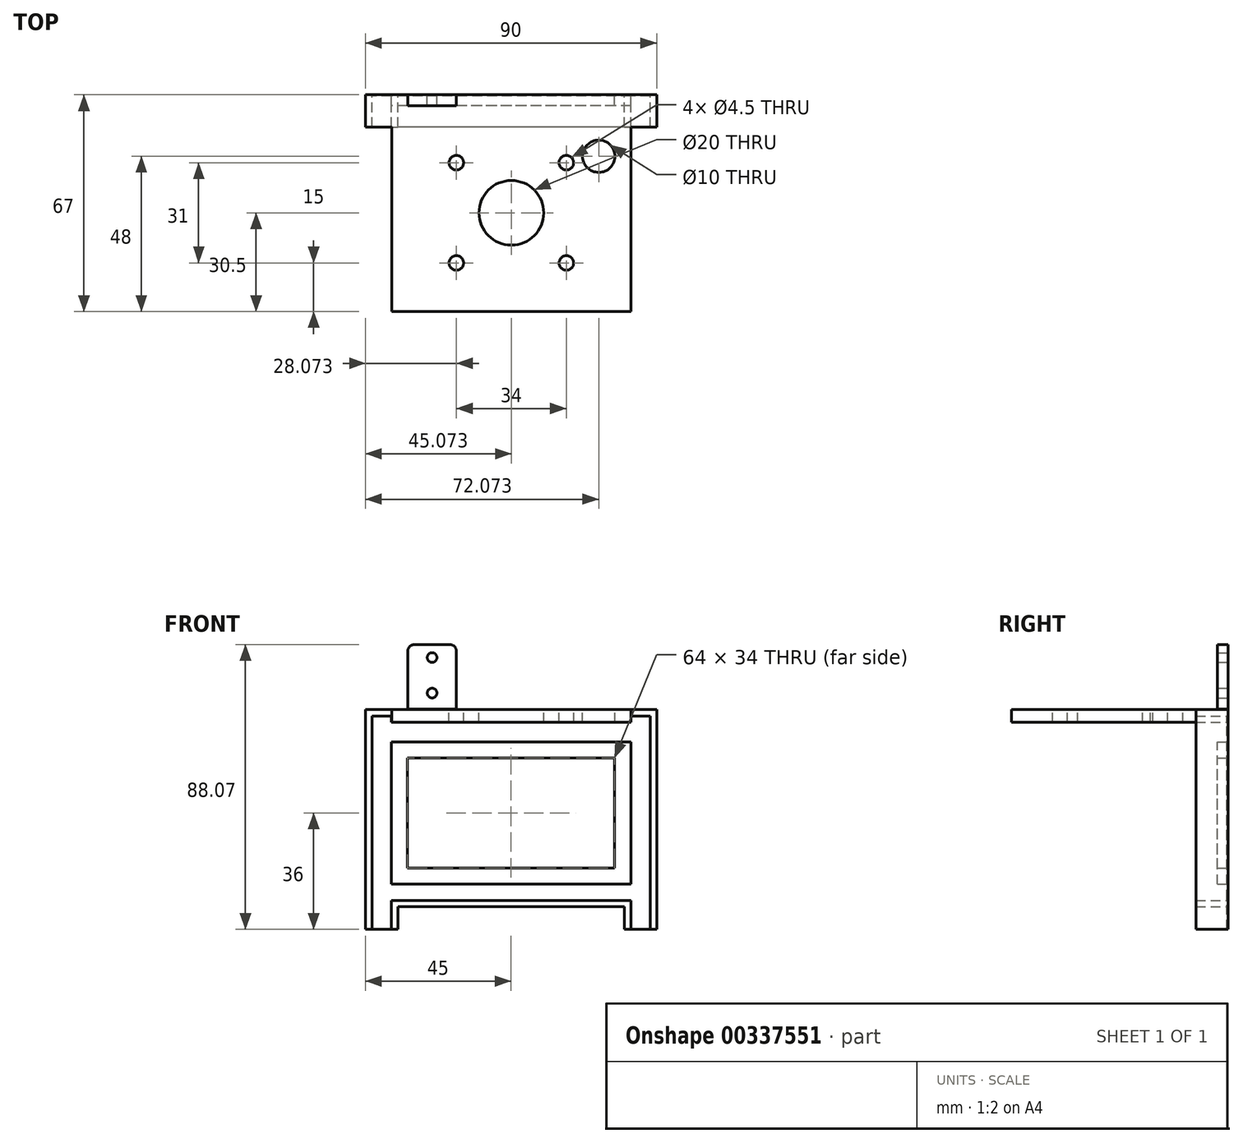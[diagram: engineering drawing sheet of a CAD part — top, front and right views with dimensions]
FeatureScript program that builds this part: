
annotation { "Feature Type Name" : "Feature", "Feature Type Description" : "" }
export const myFeature = defineFeature(function(context is Context, id is Id, definition is map)
    precondition{}
    {
        {
            var Q0;
            Q0=qCreatedBy(makeId("Front.planeOp"),FACE);
            var sketch = newSketch(context, id + "F0", { "sketchPlane" : qUnion([Q0])});
            skLineSegment(sketch, "E0.bottom", {"start": v(-6, -55) * mm, "end": v(-80, -55) * mm});
            skLineSegment(sketch, "E0.top", {"start": v(-6, 0) * mm, "end": v(-80, 0) * mm});
            skLineSegment(sketch, "E0.left", {"start": v(0, -64) * mm, "end": v(0, 2) * mm});
            skLineSegment(sketch, "E0.right", {"start": v(-86, -64) * mm, "end": v(-86, 2) * mm});
            skLineSegment(sketch, "E1.0", {"start": v(0, 2) * mm, "end": v(-6, 2) * mm});
            skLineSegment(sketch, "E2.0", {"start": v(-80, -64) * mm, "end": v(-80, -55) * mm});
            skLineSegment(sketch, "E3.0", {"start": v(-6, -50) * mm, "end": v(-80, -50) * mm});
            skLineSegment(sketch, "E4.0", {"start": v(-6, -64) * mm, "end": v(-6, -55) * mm});
            skLineSegment(sketch, "E5.0", {"start": v(-6, -6) * mm, "end": v(-80, -6) * mm});
            skLineSegment(sketch, "E6.0", {"start": v(0, -64) * mm, "end": v(-6, -64) * mm});
            skPoint(sketch, "E7.orphan", {"position": v(-86, 0) * mm});
            skLineSegment(sketch, "E8.trimOffspring", {"start": v(-80, 2) * mm, "end": v(-86, 2) * mm});
            skLineSegment(sketch, "E9.trimOffspring", {"start": v(-80, 0) * mm, "end": v(-80, 2) * mm});
            skLineSegment(sketch, "E10.trimOffspring", {"start": v(-6, 0) * mm, "end": v(-6, 2) * mm});
            skLineSegment(sketch, "E11.trimOffspring", {"start": v(-80, -50) * mm, "end": v(-80, -6) * mm});
            skLineSegment(sketch, "E12.trimOffspring", {"start": v(-6, -50) * mm, "end": v(-6, -6) * mm});
            skPoint(sketch, "E13.orphan", {"position": v(0, -55) * mm});
            skLineSegment(sketch, "E14.trimOffspring", {"start": v(-80, -64) * mm, "end": v(-86, -64) * mm});
            skLineSegment(sketch, "E15.0", {"start": v(-11, -11) * mm, "end": v(-75, -11) * mm});
            skLineSegment(sketch, "E16.0", {"start": v(-75, -45) * mm, "end": v(-75, -11) * mm});
            skLineSegment(sketch, "E17.0", {"start": v(-11, -45) * mm, "end": v(-11, -11) * mm});
            skLineSegment(sketch, "E18.0", {"start": v(-11, -45) * mm, "end": v(-75, -45) * mm});
            skLineSegment(sketch, "E19.0", {"start": v(-88, -64) * mm, "end": v(-88, 4) * mm});
            skLineSegment(sketch, "E20.0", {"start": v(2, -64) * mm, "end": v(2, 4) * mm});
            skLineSegment(sketch, "E21.0", {"start": v(-8, -57) * mm, "end": v(-78, -57) * mm});
            skLineSegment(sketch, "E22.0", {"start": v(-78, -64) * mm, "end": v(-78, -57) * mm});
            skLineSegment(sketch, "E23.0", {"start": v(-8, -64) * mm, "end": v(-8, -57) * mm});
            skLineSegment(sketch, "E24.0", {"start": v(2, 4) * mm, "end": v(-88, 4) * mm});
            skLineSegment(sketch, "E25", {"start": v(-88, -64) * mm, "end": v(-86, -64) * mm});
            skLineSegment(sketch, "E26", {"start": v(-80, -64) * mm, "end": v(-78, -64) * mm});
            skLineSegment(sketch, "E27", {"start": v(-8, -64) * mm, "end": v(-6, -64) * mm});
            skLineSegment(sketch, "E28", {"start": v(0, -64) * mm, "end": v(2, -64) * mm});
            skLineSegment(sketch, "E29", {"start": v(-43, 4) * mm, "end": v(-43, -6) * mm, "construction": true});
            skLineSegment(sketch, "E30.trimOffspring", {"start": v(-43, -11) * mm, "end": v(-43, -45) * mm, "construction": true});
            skLineSegment(sketch, "E31.trimOffspring", {"start": v(-43, -50) * mm, "end": v(-43, -57) * mm, "construction": true});
            skLineSegment(sketch, "E32", {"start": v(-43, -28) * mm, "end": v(-11, -28) * mm, "construction": true});
            skLineSegment(sketch, "E33", {"start": v(-43, -28) * mm, "end": v(-75, -28) * mm, "construction": true});
            skSolve(sketch);
        }
        {
            var Q0;
            Q0=qCreatedBy(makeId("Front.planeOp"),FACE);
            var sketch = newSketch(context, id + "F1", { "sketchPlane" : qUnion([Q0])});
            skSolve(sketch);
        }
        {
            var Q0;
            Q0=makeQuery(id+"F0.imprint","IMPRINT",FACE,{"disambiguationData":[TD([[makeQuery(id+"F0.imprint","IMPRINT",EDGE,{"derivedFrom":sQuery(id+"F0.wireOp",EDGE,"E0.top")}),-1.0]])]});
            var Q1;
            Q1=makeQuery(id+"F0.imprint","IMPRINT",FACE,{"disambiguationData":[TD([[makeQuery(id+"F0.imprint","IMPRINT",EDGE,{"derivedFrom":sQuery(id+"F0.wireOp",EDGE,"E0.bottom")}),1.0]])]});
            extrude(context, id + "F2", {"entities" : qUnion([Q0, Q1]), "depth" : 10 * mm, "offsetDistance" : 25 * mm});
        }
        {
            var Q0;
            Q0=makeQuery(id+"F2.opExtrude","CAP_FACE",FACE,{"disambiguationData":[OSD([sQuery(id+"F0.wireOp",EDGE,"E0.top"),sQuery(id+"F0.wireOp",EDGE,"E0.left"),sQuery(id+"F0.wireOp",EDGE,"E0.right"),sQuery(id+"F0.wireOp",EDGE,"E1.0"),sQuery(id+"F0.wireOp",EDGE,"E8.trimOffspring"),sQuery(id+"F0.wireOp",EDGE,"E9.trimOffspring"),sQuery(id+"F0.wireOp",EDGE,"E10.trimOffspring"),sQuery(id+"F0.wireOp",EDGE,"a58f2442-799a-4d81-9ace-714ee580b7c8.0"),sQuery(id+"F0.wireOp",EDGE,"7c9e68e3-580b-48e5-8064-8f0ad7c2d5c0.trimOffspring"),sQuery(id+"F0.wireOp",EDGE,"E19.0"),sQuery(id+"F0.wireOp",EDGE,"E20.0"),sQuery(id+"F0.wireOp",EDGE,"E24.0"),sQuery(id+"F0.wireOp",EDGE,"E25"),sQuery(id+"F0.wireOp",EDGE,"E28")])],"isStart":false});
            var sketch = newSketch(context, id + "F3", { "sketchPlane" : qUnion([Q0])});
            skLineSegment(sketch, "E34.0", {"start": v(-5.93, 0) * mm, "end": v(-79.93, 0) * mm});
            skLineSegment(sketch, "E35.0", {"start": v(-5.93, 4) * mm, "end": v(-79.93, 4) * mm});
            skPoint(sketch, "E36.0", {"position": v(-5.93, 0.8) * mm});
            skLineSegment(sketch, "E37", {"start": v(-5.93, 0) * mm, "end": v(-5.93, 4) * mm});
            skPoint(sketch, "E38.orphan", {"position": v(2, 4) * mm});
            skPoint(sketch, "E39.orphan", {"position": v(-88, 4) * mm});
            skLineSegment(sketch, "E40", {"start": v(-79.93, 4) * mm, "end": v(-79.93, 0) * mm});
            skSolve(sketch);
        }
        {
            var Q0;
            Q0=makeQuery(id+"FJxWL17Nk6DXdg4_4.boolean.opBoolean","MERGE",FACE,{"derivedFrom":[makeQuery(id+"F2.opExtrude","SWEPT_FACE",FACE,{"disambiguationData":[OSD([sQuery(id+"F0.wireOp",EDGE,"E24.0")])]}),makeQuery(id+"FJxWL17Nk6DXdg4_4.opExtrude","SWEPT_FACE",FACE,{"disambiguationData":[OSD([sQuery(id+"F3.wireOp",EDGE,"E35.0")])]})]});
            var sketch = newSketch(context, id + "F4", { "sketchPlane" : qUnion([Q0])});
            skLineSegment(sketch, "E41.1", {"start": v(-5.93, -67) * mm, "end": v(-5.93, -10) * mm});
            skLineSegment(sketch, "E41.2", {"start": v(-79.93, -67) * mm, "end": v(-79.93, -10) * mm});
            skLineSegment(sketch, "E42", {"start": v(-79.93, -10) * mm, "end": v(-5.93, -10) * mm});
            skCircle(sketch, "E43", {"center": v(-42.93, -36.5) * mm, "radius": 10 * mm});
            skLineSegment(sketch, "E44.0", {"start": v(-59.93, -52) * mm, "end": v(-59.93, -21) * mm, "construction": true});
            skLineSegment(sketch, "E45.0", {"start": v(-25.93, -52) * mm, "end": v(-25.93, -21) * mm, "construction": true});
            skLineSegment(sketch, "E46.0", {"start": v(-5.93, -67) * mm, "end": v(-79.93, -67) * mm});
            skLineSegment(sketch, "E47.0", {"start": v(-25.93, -52) * mm, "end": v(-59.93, -52) * mm, "construction": true});
            skLineSegment(sketch, "E48.0", {"start": v(-5.93, -23) * mm, "end": v(-79.93, -23) * mm, "construction": true});
            skLineSegment(sketch, "E49.0", {"start": v(-5.93, -15) * mm, "end": v(-79.93, -15) * mm, "construction": true});
            skLineSegment(sketch, "E50.trimOffspring", {"start": v(-15.93, -23) * mm, "end": v(-15.93, -15) * mm, "construction": true});
            skLineSegment(sketch, "E51.trimOffspring", {"start": v(-25.93, -21) * mm, "end": v(-59.93, -21) * mm, "construction": true});
            skLineSegment(sketch, "E52.trimOffspring", {"start": v(-25.93, -15) * mm, "end": v(-25.93, -10) * mm, "construction": true});
            skLineSegment(sketch, "E53.trimOffspring", {"start": v(-59.93, -15) * mm, "end": v(-59.93, -10) * mm, "construction": true});
            skPoint(sketch, "E54.orphan", {"position": v(-79.93, -21) * mm});
            skPoint(sketch, "E55.orphan", {"position": v(-84.93, -52) * mm});
            skPoint(sketch, "E56.orphan", {"position": v(-59.93, -67) * mm});
            skPoint(sketch, "E57.orphan", {"position": v(-25.93, -67) * mm});
            skPoint(sketch, "E58.orphan", {"position": v(-5.93, -52) * mm});
            skLineSegment(sketch, "E59", {"start": v(-59.93, -21) * mm, "end": v(-25.93, -52) * mm, "construction": true});
            skLineSegment(sketch, "E60", {"start": v(-59.93, -52) * mm, "end": v(-25.93, -21) * mm, "construction": true});
            skCircle(sketch, "E61", {"center": v(-59.93, -21) * mm, "radius": 2.25 * mm});
            skCircle(sketch, "E62", {"center": v(-59.93, -52) * mm, "radius": 2.25 * mm});
            skCircle(sketch, "E63", {"center": v(-25.93, -52) * mm, "radius": 2.25 * mm});
            skCircle(sketch, "E64", {"center": v(-25.93, -21) * mm, "radius": 2.25 * mm});
            skCircle(sketch, "E65", {"center": v(-15.93, -19) * mm, "radius": 5 * mm});
            skSolve(sketch);
        }
        {
            var Q0;
            Q0=makeQuery(id+"F4.imprint","IMPRINT",FACE,{"disambiguationData":[TD([[makeQuery(id+"F4.imprint","IMPRINT",EDGE,{"derivedFrom":sQuery(id+"F4.wireOp",EDGE,"E41.1")}),1.0]])]});
            var Q1;
            Q1=makeQuery(id+"F2.opExtrude","SWEPT_FACE",FACE,{"disambiguationData":[OSD([sQuery(id+"F0.wireOp",EDGE,"E0.top")])]});
            extrude(context, id + "F5", {"entities" : qUnion([Q0]), "operationType" : NewBodyOperationType.ADD, "endBound" : BoundingType.UP_TO_SURFACE, "oppositeDirection" : true, "endBoundEntityFace" : qUnion([Q1]), "depth" : 25 * mm, "offsetDistance" : 25 * mm});
        }
        {
            var Q0;
            Q0=makeQuery(id+"F0.imprint","IMPRINT",FACE,{"disambiguationData":[TD([[makeQuery(id+"F0.imprint","IMPRINT",EDGE,{"derivedFrom":sQuery(id+"F0.wireOp",EDGE,"E0.bottom")}),-1.0]])]});
            extrude(context, id + "F6", {"entities" : qUnion([Q0]), "operationType" : NewBodyOperationType.ADD, "depth" : 0.4 * mm, "offsetDistance" : 25 * mm});
        }
        {
            var Q0;
            Q0=makeQuery(id+"F0.imprint","IMPRINT",FACE,{"disambiguationData":[TD([[makeQuery(id+"F0.imprint","IMPRINT",EDGE,{"derivedFrom":sQuery(id+"F0.wireOp",EDGE,"E3.0")}),-1.0]])]});
            extrude(context, id + "F7", {"entities" : qUnion([Q0]), "operationType" : NewBodyOperationType.ADD, "depth" : 3.4 * mm, "offsetDistance" : 25 * mm});
        }
        {
            var Q0;
            Q0=qCreatedBy(makeId("Front.planeOp"),FACE);
            var sketch = newSketch(context, id + "F8", { "sketchPlane" : qUnion([Q0])});
            skLineSegment(sketch, "E66", {"start": v(-59.93, 4.07) * mm, "end": v(-59.93, 22.07) * mm});
            skLineSegment(sketch, "E67.0", {"start": v(-74.93, 4.07) * mm, "end": v(-74.93, 22.07) * mm});
            skLineSegment(sketch, "E68", {"start": v(-72.93, 24.07) * mm, "end": v(-61.93, 24.07) * mm});
            skLineSegment(sketch, "E69", {"start": v(-74.93, 4.07) * mm, "end": v(-59.93, 4.07) * mm});
            skLineSegment(sketch, "E70", {"start": v(-67.43, 24.07) * mm, "end": v(-67.43, 4.07) * mm, "construction": true});
            skLineSegment(sketch, "E71.0", {"start": v(-74.93, 9.07) * mm, "end": v(-59.93, 9.07) * mm, "construction": true});
            skLineSegment(sketch, "E72.0", {"start": v(-74.93, 20.07) * mm, "end": v(-59.93, 20.07) * mm, "construction": true});
            skCircle(sketch, "E73", {"center": v(-67.43, 20.07) * mm, "radius": 1.5 * mm});
            skCircle(sketch, "E74", {"center": v(-67.43, 9.07) * mm, "radius": 1.5 * mm});
            skPoint(sketch, "E75.visualSharp", {"position": v(-74.93, 24.07) * mm});
            skArc(sketch, "E75.filletArc", {"start": v(-72.93, 24.07) * mm, "mid": v(-74.34, 23.49) * mm, "end": v(-74.93, 22.07) * mm});
            skPoint(sketch, "E76.visualSharp", {"position": v(-59.93, 24.07) * mm});
            skArc(sketch, "E76.filletArc", {"start": v(-59.93, 22.07) * mm, "mid": v(-60.51, 23.49) * mm, "end": v(-61.93, 24.07) * mm});
            skSolve(sketch);
        }
        {
            var Q0;
            Q0 = qSketchRegion(id + "F8", true);
            extrude(context, id + "F9", {"entities" : qUnion([Q0]), "operationType" : NewBodyOperationType.ADD, "depth" : 3.4 * mm, "offsetDistance" : 25 * mm});
        }
    });
